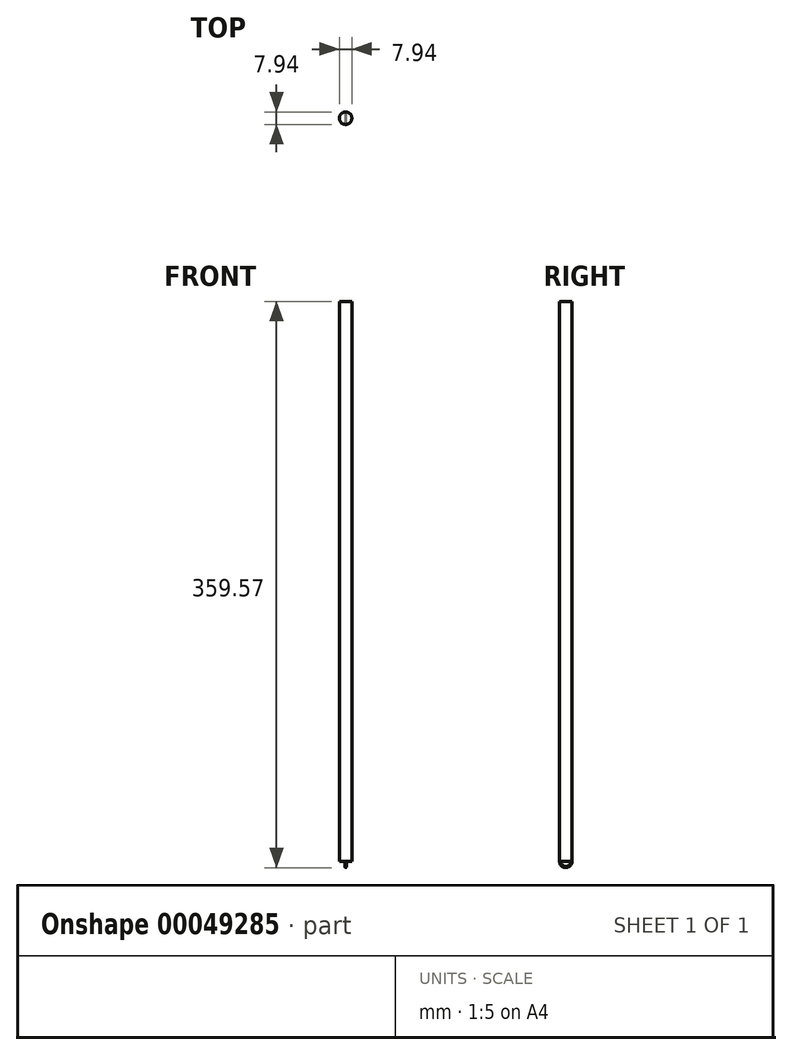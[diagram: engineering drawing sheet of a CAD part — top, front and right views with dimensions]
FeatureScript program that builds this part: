
annotation { "Feature Type Name" : "Feature", "Feature Type Description" : "" }
export const myFeature = defineFeature(function(context is Context, id is Id, definition is map)
    precondition{}
    {
        {
            var Q0;
            Q0=qCreatedBy(makeId("Top.planeOp"),FACE);
            var sketch = newSketch(context, id + "F0", { "sketchPlane" : qUnion([Q0])});
            skCircle(sketch, "E0", {"center": v(0, 0) * mm, "radius": 3.97 * mm});
            skSolve(sketch);
        }
        {
            var Q0;
            Q0=makeQuery(id+"F0.imprint","IMPRINT",FACE,{"disambiguationData":[TD([[makeQuery(id+"F0.imprint","IMPRINT",EDGE,{"derivedFrom":sQuery(id+"F0.wireOp",EDGE,"E0")}),1.0]])]});
            extrude(context, id + "F1", {"entities" : qUnion([Q0]), "depth" : 355.6 * mm});
        }
        {
            var Q0;
            Q0=qCreatedBy(makeId("Top.planeOp"),FACE);
            var sketch = newSketch(context, id + "F2", { "sketchPlane" : qUnion([Q0])});
            skCircle(sketch, "E1", {"center": v(0, -3.57) * mm, "radius": 0.4 * mm});
            skLineSegment(sketch, "E2", {"start": v(-3.98, 0) * mm, "end": v(4.05, 0) * mm, "construction": true});
            skSolve(sketch);
        }
        {
            var Q0;
            Q0 = qSketchRegion(id + "F2", true);
            var Q1;
            Q1=sQuery(id+"F2.wireOp",EDGE,"E2");
            revolve(context, id + "F3", {"operationType" : NewBodyOperationType.ADD, "entities" : qUnion([Q0]), "axis" : qUnion([Q1]), "revolveType" : RevolveType.FULL});
        }
    });
